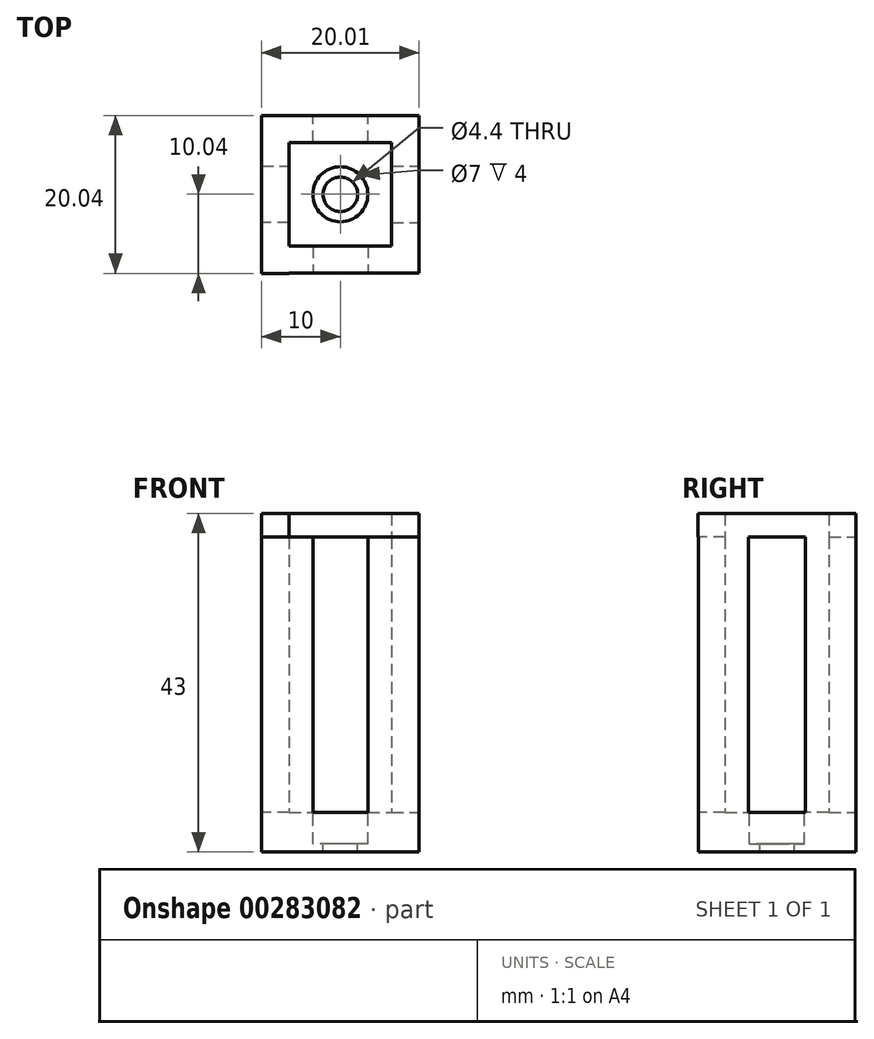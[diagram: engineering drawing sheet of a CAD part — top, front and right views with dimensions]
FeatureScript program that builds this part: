
annotation { "Feature Type Name" : "Feature", "Feature Type Description" : "" }
export const myFeature = defineFeature(function(context is Context, id is Id, definition is map)
    precondition{}
    {
        {
            var Q0;
            Q0=qCreatedBy(makeId("Top.planeOp"),FACE);
            var sketch = newSketch(context, id + "F0", { "sketchPlane" : qUnion([Q0])});
            skLineSegment(sketch, "E0.bottom", {"start": v(10, -10) * mm, "end": v(-10, -10) * mm});
            skLineSegment(sketch, "E0.top", {"start": v(10, 10) * mm, "end": v(-10, 10) * mm});
            skLineSegment(sketch, "E0.left", {"start": v(10, -10) * mm, "end": v(10, 10) * mm});
            skLineSegment(sketch, "E0.right", {"start": v(-10, -10) * mm, "end": v(-10, 10) * mm});
            skPoint(sketch, "E0.middle", {"position": v(0, 0) * mm});
            skSolve(sketch);
        }
        {
            var Q0;
            Q0=makeQuery(id+"F0.imprint","IMPRINT",FACE,{"disambiguationData":[TD([[makeQuery(id+"F0.imprint","IMPRINT",EDGE,{"derivedFrom":sQuery(id+"F0.wireOp",EDGE,"E0.bottom")}),-1.0]])]});
            extrude(context, id + "F1", {"entities" : qUnion([Q0]), "depth" : 5 * mm});
        }
        {
            var Q0;
            Q0=makeQuery(id+"F1.opExtrude","CAP_FACE",FACE,{"disambiguationData":[OSD([sQuery(id+"F0.wireOp",EDGE,"E0.bottom"),sQuery(id+"F0.wireOp",EDGE,"E0.top"),sQuery(id+"F0.wireOp",EDGE,"E0.left"),sQuery(id+"F0.wireOp",EDGE,"E0.right")])],"isStart":false});
            var sketch = newSketch(context, id + "F2", { "sketchPlane" : qUnion([Q0])});
            skPoint(sketch, "E1", {"position": v(0, 0) * mm});
            skSolve(sketch);
        }
        {
            var Q0;
            Q0=sQuery(id+"F2.wireOp",VERTEX,"E1");
            var Q1;
            Q1=makeQuery(id+"F1.opExtrude","SWEPT_BODY",BODY,{"disambiguationData":[OSD([sQuery(id+"F0.wireOp",EDGE,"E0.bottom"),sQuery(id+"F0.wireOp",EDGE,"E0.top"),sQuery(id+"F0.wireOp",EDGE,"E0.left"),sQuery(id+"F0.wireOp",EDGE,"E0.right")])]});
            hole(context, id + "F3", {"style" : HoleStyle.SIMPLE, "endStyle" : HoleEndStyle.THROUGH, "standardTappedOrClearance" : lookupTablePath({ "standard" : "ISO", "fit" : "Normal", "size" : "M4", "type" : "Clearance" }), "standardBlindInLast" : lookupTablePath({ "fit" : "Standard", "standard" : "ISO", "size" : "M4", "type" : "Clearance" }), "holeDiameter" : 4.4 * mm, "tappedDepth" : 12 * mm, "tapClearance" : 3, "locations" : qUnion([Q0]), "scope" : qUnion([Q1])});
        }
        {
            var Q0;
            Q0=makeQuery(id+"F1.opExtrude","CAP_FACE",FACE,{"disambiguationData":[OSD([sQuery(id+"F0.wireOp",EDGE,"E0.bottom"),sQuery(id+"F0.wireOp",EDGE,"E0.top"),sQuery(id+"F0.wireOp",EDGE,"E0.left"),sQuery(id+"F0.wireOp",EDGE,"E0.right")])],"isStart":false});
            var sketch = newSketch(context, id + "F4", { "sketchPlane" : qUnion([Q0])});
            skPoint(sketch, "E2.middle", {"position": v(0, 0) * mm});
            skLineSegment(sketch, "E3.bottom", {"start": v(-6.5, 6.6) * mm, "end": v(-10, 6.6) * mm});
            skLineSegment(sketch, "E3.top", {"start": v(-6.5, 10) * mm, "end": v(-10, 10) * mm});
            skLineSegment(sketch, "E3.left", {"start": v(-6.5, 6.6) * mm, "end": v(-6.5, 10) * mm});
            skLineSegment(sketch, "E3.right", {"start": v(-10, 6.6) * mm, "end": v(-10, 10) * mm});
            skLineSegment(sketch, "E4.bottom", {"start": v(6.5, 6.6) * mm, "end": v(10, 6.6) * mm});
            skLineSegment(sketch, "E4.top", {"start": v(6.5, 10) * mm, "end": v(10, 10) * mm});
            skLineSegment(sketch, "E4.left", {"start": v(6.5, 6.6) * mm, "end": v(6.5, 10) * mm});
            skLineSegment(sketch, "E4.right", {"start": v(10, 6.6) * mm, "end": v(10, 10) * mm});
            skLineSegment(sketch, "E5.bottom", {"start": v(6.5, -6.6) * mm, "end": v(10, -6.6) * mm});
            skLineSegment(sketch, "E5.top", {"start": v(6.5, -10) * mm, "end": v(10, -10) * mm});
            skLineSegment(sketch, "E5.left", {"start": v(6.5, -6.6) * mm, "end": v(6.5, -10) * mm});
            skLineSegment(sketch, "E5.right", {"start": v(10, -6.6) * mm, "end": v(10, -10) * mm});
            skLineSegment(sketch, "E6.bottom", {"start": v(-6.5, -6.6) * mm, "end": v(-10, -6.6) * mm});
            skLineSegment(sketch, "E6.top", {"start": v(-6.5, -10) * mm, "end": v(-10, -10) * mm});
            skLineSegment(sketch, "E6.left", {"start": v(-6.5, -6.6) * mm, "end": v(-6.5, -10) * mm});
            skLineSegment(sketch, "E6.right", {"start": v(-10, -6.6) * mm, "end": v(-10, -10) * mm});
            skLineSegment(sketch, "E7.bottom", {"start": v(-10, 6.6) * mm, "end": v(-6.5, 6.6) * mm});
            skLineSegment(sketch, "E7.top", {"start": v(-10, 3.6) * mm, "end": v(-6.5, 3.6) * mm});
            skLineSegment(sketch, "E7.left", {"start": v(-10, 6.6) * mm, "end": v(-10, 3.6) * mm});
            skLineSegment(sketch, "E7.right", {"start": v(-6.5, 6.6) * mm, "end": v(-6.5, 3.6) * mm});
            skLineSegment(sketch, "E8.top", {"start": v(-6.5, -3.6) * mm, "end": v(-10, -3.6) * mm});
            skLineSegment(sketch, "E8.left", {"start": v(-6.5, -6.6) * mm, "end": v(-6.5, -3.6) * mm});
            skLineSegment(sketch, "E8.right", {"start": v(-10, -6.6) * mm, "end": v(-10, -3.6) * mm});
            skLineSegment(sketch, "E9.bottom", {"start": v(-6.5, -6.6) * mm, "end": v(-3.5, -6.6) * mm});
            skLineSegment(sketch, "E9.top", {"start": v(-6.5, -10) * mm, "end": v(-3.5, -10) * mm});
            skLineSegment(sketch, "E9.right", {"start": v(-3.5, -6.6) * mm, "end": v(-3.5, -10) * mm});
            skLineSegment(sketch, "E10.bottom", {"start": v(3.5, -6.6) * mm, "end": v(6.5, -6.6) * mm});
            skLineSegment(sketch, "E10.top", {"start": v(3.5, -10) * mm, "end": v(6.5, -10) * mm});
            skLineSegment(sketch, "E10.left", {"start": v(3.5, -6.6) * mm, "end": v(3.5, -10) * mm});
            skLineSegment(sketch, "E11.top", {"start": v(6.5, -3.6) * mm, "end": v(10, -3.6) * mm});
            skLineSegment(sketch, "E11.left", {"start": v(6.5, -6.6) * mm, "end": v(6.5, -3.6) * mm});
            skLineSegment(sketch, "E11.right", {"start": v(10, -6.6) * mm, "end": v(10, -3.6) * mm});
            skLineSegment(sketch, "E12.top", {"start": v(6.5, 3.6) * mm, "end": v(10, 3.6) * mm});
            skLineSegment(sketch, "E12.left", {"start": v(6.5, 6.6) * mm, "end": v(6.5, 3.6) * mm});
            skLineSegment(sketch, "E12.right", {"start": v(10, 6.6) * mm, "end": v(10, 3.6) * mm});
            skLineSegment(sketch, "E13.bottom", {"start": v(6.5, 6.6) * mm, "end": v(3.5, 6.6) * mm});
            skLineSegment(sketch, "E13.top", {"start": v(6.5, 10) * mm, "end": v(3.5, 10) * mm});
            skLineSegment(sketch, "E13.right", {"start": v(3.5, 6.6) * mm, "end": v(3.5, 10) * mm});
            skLineSegment(sketch, "E14.bottom", {"start": v(-6.5, 6.6) * mm, "end": v(-3.5, 6.6) * mm});
            skLineSegment(sketch, "E14.top", {"start": v(-6.5, 10) * mm, "end": v(-3.5, 10) * mm});
            skLineSegment(sketch, "E14.right", {"start": v(-3.5, 6.6) * mm, "end": v(-3.5, 10) * mm});
            skSolve(sketch);
        }
        {
            var Q0;
            Q0 = qSketchRegion(id + "F4", true);
            extrude(context, id + "F5", {"entities" : qUnion([Q0]), "operationType" : NewBodyOperationType.ADD, "depth" : 35 * mm});
        }
        {
            var Q0;
            Q0=makeQuery(id+"F5.opExtrude","CAP_FACE",FACE,{"disambiguationData":[OSD([sQuery(id+"F4.wireOp",EDGE,"E3.top"),sQuery(id+"F4.wireOp",EDGE,"E3.right"),sQuery(id+"F4.wireOp",EDGE,"E7.top"),sQuery(id+"F4.wireOp",EDGE,"E7.left"),sQuery(id+"F4.wireOp",EDGE,"E7.right"),sQuery(id+"F4.wireOp",EDGE,"E14.bottom"),sQuery(id+"F4.wireOp",EDGE,"E14.top"),sQuery(id+"F4.wireOp",EDGE,"E14.right")])],"isStart":false});
            var sketch = newSketch(context, id + "F6", { "sketchPlane" : qUnion([Q0])});
            skLineSegment(sketch, "E15", {"start": v(-6.17, 6.27) * mm, "end": v(-6.2, 6.27) * mm});
            skLineSegment(sketch, "E16", {"start": v(-6.18, 12.5) * mm, "end": v(-6.2, 12.5) * mm});
            skLineSegment(sketch, "E17.bottom", {"start": v(-10, 10) * mm, "end": v(-6.5, 10) * mm});
            skLineSegment(sketch, "E17.top", {"start": v(-10, -10.04) * mm, "end": v(-6.5, -10.04) * mm});
            skLineSegment(sketch, "E17.left", {"start": v(-10, 10) * mm, "end": v(-10, -10.04) * mm});
            skLineSegment(sketch, "E17.right", {"start": v(-6.5, 10) * mm, "end": v(-6.5, -10.04) * mm});
            skLineSegment(sketch, "E18.bottom", {"start": v(10, 10) * mm, "end": v(6.5, 10) * mm});
            skLineSegment(sketch, "E18.top", {"start": v(10, 1.06) * mm, "end": v(6.5, 1.06) * mm});
            skLineSegment(sketch, "E18.left", {"start": v(10, 10) * mm, "end": v(10, 1.06) * mm});
            skLineSegment(sketch, "E18.right", {"start": v(6.5, 10) * mm, "end": v(6.5, 1.06) * mm});
            skLineSegment(sketch, "E19.bottom", {"start": v(6.5, 1.06) * mm, "end": v(10, 1.06) * mm});
            skLineSegment(sketch, "E19.top", {"start": v(6.5, -10.01) * mm, "end": v(10, -10.01) * mm});
            skLineSegment(sketch, "E19.left", {"start": v(6.5, 1.06) * mm, "end": v(6.5, -10.01) * mm});
            skLineSegment(sketch, "E19.right", {"start": v(10, 1.06) * mm, "end": v(10, -10.01) * mm});
            skLineSegment(sketch, "E20.bottom", {"start": v(6.5, -10.01) * mm, "end": v(-6.5, -10.01) * mm});
            skLineSegment(sketch, "E20.top", {"start": v(6.5, -6.6) * mm, "end": v(-6.5, -6.6) * mm});
            skLineSegment(sketch, "E20.left", {"start": v(6.5, -10.01) * mm, "end": v(6.5, -6.6) * mm});
            skLineSegment(sketch, "E20.right", {"start": v(-6.5, -10.01) * mm, "end": v(-6.5, -6.6) * mm});
            skLineSegment(sketch, "E21.bottom", {"start": v(-6.5, 6.6) * mm, "end": v(6.5, 6.6) * mm});
            skLineSegment(sketch, "E21.top", {"start": v(-6.5, 10) * mm, "end": v(6.5, 10) * mm});
            skLineSegment(sketch, "E21.left", {"start": v(-6.5, 6.6) * mm, "end": v(-6.5, 10) * mm});
            skLineSegment(sketch, "E21.right", {"start": v(6.5, 6.6) * mm, "end": v(6.5, 10) * mm});
            skSolve(sketch);
        }
        {
            var Q0;
            Q0 = qSketchRegion(id + "F6", true);
            extrude(context, id + "F7", {"entities" : qUnion([Q0]), "operationType" : NewBodyOperationType.ADD, "depth" : 1 * mm});
        }
        {
            var Q0;
            Q0=makeQuery(id+"F1.opExtrude","CAP_FACE",FACE,{"disambiguationData":[OSD([sQuery(id+"F0.wireOp",EDGE,"E0.bottom"),sQuery(id+"F0.wireOp",EDGE,"E0.top"),sQuery(id+"F0.wireOp",EDGE,"E0.left"),sQuery(id+"F0.wireOp",EDGE,"E0.right")])],"isStart":false});
            var sketch = newSketch(context, id + "F8", { "sketchPlane" : qUnion([Q0])});
            skPoint(sketch, "E22", {"position": v(0, 0) * mm});
            skSolve(sketch);
        }
        {
            var Q0;
            Q0=makeQuery(id+"F8.imprint","IMPRINT",FACE,{"disambiguationData":[TD([[makeQuery(id+"F8.imprint","IMPRINT",EDGE,{"derivedFrom":makeQuery(id+"F1.opExtrude","CAP_EDGE",EDGE,{"disambiguationData":[OSD([sQuery(id+"F0.wireOp",EDGE,"E0.bottom")])],"isStart":false})}),-1.0]])]});
            var sketch = newSketch(context, id + "F9", { "sketchPlane" : qUnion([Q0])});
            skCircle(sketch, "E23", {"center": v(0, 0) * mm, "radius": 3.5 * mm});
            skSolve(sketch);
        }
        {
            var Q0;
            Q0 = qSketchRegion(id + "F9", true);
            extrude(context, id + "F10", {"entities" : qUnion([Q0]), "operationType" : NewBodyOperationType.REMOVE, "oppositeDirection" : true, "depth" : 4 * mm});
        }
        {
            var Q0;
            Q0=makeQuery(id+"F7.opExtrude","CAP_FACE",FACE,{"disambiguationData":[OSD([sQuery(id+"F6.wireOp",EDGE,"E17.bottom"),sQuery(id+"F6.wireOp",EDGE,"E17.top"),sQuery(id+"F6.wireOp",EDGE,"E17.left"),sQuery(id+"F6.wireOp",EDGE,"E17.right"),sQuery(id+"F6.wireOp",EDGE,"E18.bottom"),sQuery(id+"F6.wireOp",EDGE,"E18.left"),sQuery(id+"F6.wireOp",EDGE,"E18.right"),sQuery(id+"F6.wireOp",EDGE,"E19.top"),sQuery(id+"F6.wireOp",EDGE,"E19.left"),sQuery(id+"F6.wireOp",EDGE,"E19.right"),sQuery(id+"F6.wireOp",EDGE,"E20.bottom"),sQuery(id+"F6.wireOp",EDGE,"E20.top"),sQuery(id+"F6.wireOp",EDGE,"E21.bottom"),sQuery(id+"F6.wireOp",EDGE,"E21.top")])],"isStart":false});
            extrude(context, id + "F11", {"entities" : qUnion([Q0]), "operationType" : NewBodyOperationType.ADD, "depth" : 2 * mm});
        }
    });
